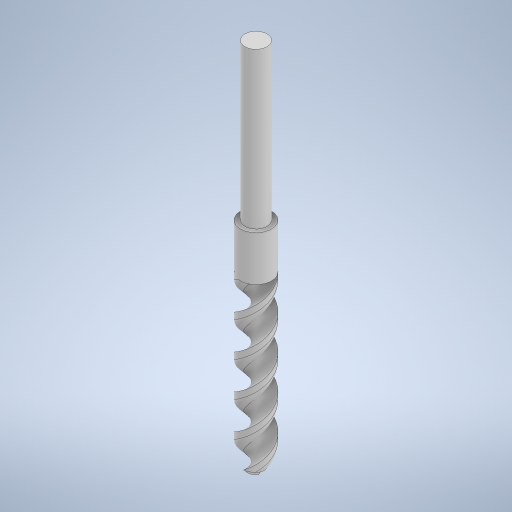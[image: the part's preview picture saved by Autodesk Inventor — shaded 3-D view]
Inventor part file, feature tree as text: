
AUTODESK INVENTOR PART (.ipt)
format: ipt  version: 2024.2 (Build 282272000, 272)  size: 637,440 bytes
history: native  units: mm
features: sketch x5, extrude x3, helix x1, pattern_circular x1, revolve x1, fillet x1
ambient origin geometry x8: Origin, YZ Plane, XZ Plane, XY Plane, X Axis, Y Axis, Z Axis, Center Point
bodies: Body1 (feature_tree)
feature tree (12):
  extrude  "Extrusion3"  Depth=60.0mm TaperAngle=0.0deg
  extrude  "Extrusion4"  Depth=3.0mm TaperAngle=0.0deg
  helix  "Coil2"  [1 undecoded]
  pattern_circular  "Circular Pattern2"  Count=2 Angle=360.0deg
  revolve  "Revolution1"  Angle=90.0deg
  fillet  "Fillet5"  Radius=1.7638mm
  extrude  "Extrusion5"  Depth=45.0mm TaperAngle=0.0deg
  sketch  "Sketch9"  dims[d25=9.0mm d26=60.0mm d27=0.0mm]
  sketch  "Sketch10"  dims[d28=5.0mm d29=3.0mm d30=0.0mm d32=7.0mm]
  sketch  "Sketch12"  dims[d33=20.0mm d34=50.0mm d35=10.0mm d36=0.0mm d37=90.0deg d38=90.0deg d39=0.0mm d40=0.0mm d41=20.0mm d42=360.0deg]
  sketch  "Sketch16"  dims[d45=1.0mm d46=90.0deg d47=1.7638mm]
  sketch  "Sketch18"  dims[d48=6.44mm d49=45.0mm d50=0.0mm d1=0.5mm d2=0.872665mm d3=0.5mm d4=0.872665mm d44=0.0mm]
note: 1 required parameter value undecoded (feature->parameter linkage not recoverable at this tier; creation-order binding heuristic only, values carry confidence <= 0.55)
